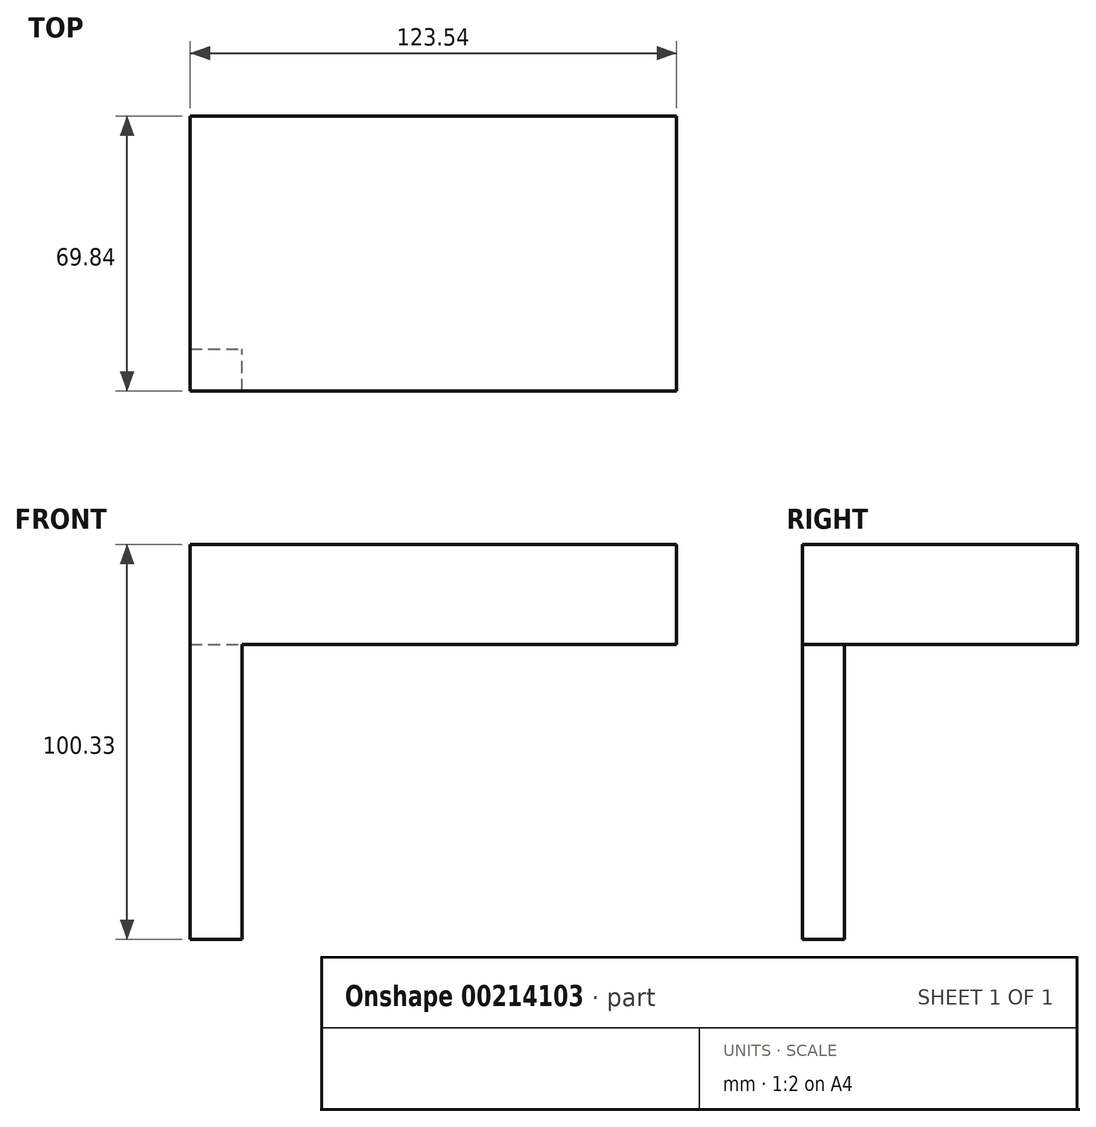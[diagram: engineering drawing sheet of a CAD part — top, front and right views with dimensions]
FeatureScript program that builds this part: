
annotation { "Feature Type Name" : "Feature", "Feature Type Description" : "" }
export const myFeature = defineFeature(function(context is Context, id is Id, definition is map)
    precondition{}
    {
        {
            var Q0;
            Q0=qCreatedBy(makeId("Top.planeOp"),FACE);
            var sketch = newSketch(context, id + "F0", { "sketchPlane" : qUnion([Q0])});
            skLineSegment(sketch, "E0.bottom", {"start": v(61.77, -34.92) * mm, "end": v(-61.77, -34.92) * mm});
            skLineSegment(sketch, "E0.top", {"start": v(61.77, 34.92) * mm, "end": v(-61.77, 34.92) * mm});
            skLineSegment(sketch, "E0.left", {"start": v(61.77, -34.92) * mm, "end": v(61.77, 34.92) * mm});
            skLineSegment(sketch, "E0.right", {"start": v(-61.77, -34.92) * mm, "end": v(-61.77, 34.92) * mm});
            skPoint(sketch, "E0.middle", {"position": v(0, 0) * mm});
            skSolve(sketch);
        }
        {
            var Q0;
            Q0=makeQuery(id+"F0.imprint","IMPRINT",FACE,{"disambiguationData":[TD([[makeQuery(id+"F0.imprint","IMPRINT",EDGE,{"derivedFrom":sQuery(id+"F0.wireOp",EDGE,"E0.bottom")}),-1.0]])]});
            extrude(context, id + "F1", {"entities" : qUnion([Q0]), "depth" : 25.4 * mm});
        }
        {
            var Q0;
            Q0=makeQuery(id+"F1.opExtrude","CAP_FACE",FACE,{"disambiguationData":[OSD([sQuery(id+"F0.wireOp",EDGE,"E0.bottom"),sQuery(id+"F0.wireOp",EDGE,"E0.top"),sQuery(id+"F0.wireOp",EDGE,"E0.left"),sQuery(id+"F0.wireOp",EDGE,"E0.right")])],"isStart":true});
            var sketch = newSketch(context, id + "F2", { "sketchPlane" : qUnion([Q0])});
            skLineSegment(sketch, "E1.bottom", {"start": v(-61.77, 34.92) * mm, "end": v(-48.57, 34.92) * mm});
            skLineSegment(sketch, "E1.top", {"start": v(-61.77, 24.29) * mm, "end": v(-48.57, 24.29) * mm});
            skLineSegment(sketch, "E1.left", {"start": v(-61.77, 34.92) * mm, "end": v(-61.77, 24.29) * mm});
            skLineSegment(sketch, "E1.right", {"start": v(-48.57, 34.92) * mm, "end": v(-48.57, 24.29) * mm});
            skSolve(sketch);
        }
        {
            var Q0;
            Q0=makeQuery(id+"F2.imprint","IMPRINT",FACE,{"disambiguationData":[TD([[makeQuery(id+"F2.imprint","IMPRINT",EDGE,{"derivedFrom":sQuery(id+"F2.wireOp",EDGE,"E1.bottom")}),1.0]])]});
            extrude(context, id + "F3", {"entities" : qUnion([Q0]), "operationType" : NewBodyOperationType.ADD, "depth" : 74.93 * mm});
        }
    });
